annotation { "Feature Type Name" : "Feature", "Feature Type Description" : "" }
export const myFeature = defineFeature(function(context is Context, id is Id, definition is map)
    precondition{}
    {
        {
            var Q0;
            Q0=qCreatedBy(makeId("Front.planeOp"),FACE);
            var sketch = newSketch(context, id + "F0", { "sketchPlane" : qUnion([Q0])});
            skLineSegment(sketch, "E0.bottom", {"start": v(-44.45, 25.4) * mm, "end": v(44.45, 25.4) * mm});
            skLineSegment(sketch, "E0.top", {"start": v(-44.45, -25.4) * mm, "end": v(44.45, -25.4) * mm});
            skLineSegment(sketch, "E0.left", {"start": v(-44.45, 25.4) * mm, "end": v(-44.45, -25.4) * mm});
            skLineSegment(sketch, "E0.right", {"start": v(44.45, 25.4) * mm, "end": v(44.45, -25.4) * mm});
            skPoint(sketch, "E0.middle", {"position": v(0, 0) * mm});
            skLineSegment(sketch, "E1", {"start": v(0, 0) * mm, "end": v(44.45, 0) * mm, "construction": true});
            skCircle(sketch, "E2", {"center": v(29.84, 10.8) * mm, "radius": 6.99 * mm});
            skCircle(sketch, "E3.0", {"center": v(29.84, 10.8) * mm, "radius": 14.6 * mm});
            skLineSegment(sketch, "E4", {"start": v(17.02, 17.78) * mm, "end": v(29.84, 17.78) * mm});
            skLineSegment(sketch, "E5", {"start": v(17.02, 17.78) * mm, "end": v(17.02, 3.81) * mm});
            skLineSegment(sketch, "E6", {"start": v(17.02, 3.81) * mm, "end": v(29.85, 3.81) * mm});
            skCircle(sketch, "E7.MirrorC", {"center": v(29.84, -10.8) * mm, "radius": 6.99 * mm});
            skLineSegment(sketch, "E8.MirrorCS", {"start": v(17.02, -17.78) * mm, "end": v(29.84, -17.78) * mm});
            skCircle(sketch, "E9.MirrorC", {"center": v(29.84, -10.8) * mm, "radius": 14.6 * mm});
            skLineSegment(sketch, "E10.MirrorCS", {"start": v(17.02, -17.78) * mm, "end": v(17.02, -3.81) * mm});
            skLineSegment(sketch, "E11.MirrorCS", {"start": v(17.02, -3.81) * mm, "end": v(29.85, -3.81) * mm});
            skSolve(sketch);
        }
        {
            var Q0;
            {var subQ5=sQuery(id+"F0.wireOp",EDGE,"E0.left");Q0=makeQuery(id+"F0.imprint","IMPRINT",FACE,{"disambiguationData":[TD([[makeQuery(id+"F0.imprint","IMPRINT",EDGE,{"derivedFrom":subQ5}),1.0]])]});}
            var Q1;
            {var subQ4=sQuery(id+"F0.wireOp",EDGE,"E4");Q1=makeQuery(id+"F0.imprint","IMPRINT",FACE,{"disambiguationData":[TD([[makeQuery(id+"F0.imprint","IMPRINT",EDGE,{"derivedFrom":subQ4}),1.0]])]});}
            var Q2;
            {var subQ0=sQuery(id+"F0.wireOp",EDGE,"E5");Q2=makeQuery(id+"F0.imprint","IMPRINT",FACE,{"disambiguationData":[TD([[makeQuery(id+"F0.imprint","IMPRINT",EDGE,{"derivedFrom":subQ0}),-1.0]])]});}
            var Q3;
            {var subQ0=sQuery(id+"F0.wireOp",EDGE,"E6");Q3=makeQuery(id+"F0.imprint","IMPRINT",FACE,{"disambiguationData":[TD([[makeQuery(id+"F0.imprint","IMPRINT",EDGE,{"derivedFrom":subQ0}),-1.0]])]});}
            var Q4;
            {var subQ0=sQuery(id+"F0.wireOp",EDGE,"E3.0");var subQ2=sQuery(id+"F0.wireOp",EDGE,"E9.MirrorC");var subQ3=makeQuery(id+"F0.imprint","INTERSECT",VERTEX,{"disambiguationData":[OD(0.0)],"derivedFrom":[subQ0,subQ2]});Q4=makeQuery(id+"F0.imprint","IMPRINT",FACE,{"disambiguationData":[TD([[makeQuery(id+"F0.imprint","IMPRINT",EDGE,{"disambiguationData":[TD([[subQ3,-1.0]])],"derivedFrom":subQ0}),1.0]])]});}
            var Q5;
            {var subQ3=sQuery(id+"F0.wireOp",EDGE,"E8.MirrorCS");Q5=makeQuery(id+"F0.imprint","IMPRINT",FACE,{"disambiguationData":[TD([[makeQuery(id+"F0.imprint","IMPRINT",EDGE,{"derivedFrom":subQ3}),-1.0]])]});}
            var Q6;
            {var subQ0=sQuery(id+"F0.wireOp",EDGE,"E11.MirrorCS");Q6=makeQuery(id+"F0.imprint","IMPRINT",FACE,{"disambiguationData":[TD([[makeQuery(id+"F0.imprint","IMPRINT",EDGE,{"derivedFrom":subQ0}),1.0]])]});}
            var Q7;
            {var subQ0=sQuery(id+"F0.wireOp",EDGE,"E10.MirrorCS");Q7=makeQuery(id+"F0.imprint","IMPRINT",FACE,{"disambiguationData":[TD([[makeQuery(id+"F0.imprint","IMPRINT",EDGE,{"derivedFrom":subQ0}),1.0]])]});}
            extrude(context, id + "F1", {"entities" : qUnion([Q0, Q1, Q2, Q3, Q4, Q5, Q6, Q7]), "depth" : 0.38 * mm});
        }
        {
            var Q0;
            Q0=makeQuery(id+"F1.opExtrude","CAP_FACE",FACE,{"disambiguationData":[OSD([sQuery(id+"F0.wireOp",EDGE,"E0.bottom"),sQuery(id+"F0.wireOp",EDGE,"E0.top"),sQuery(id+"F0.wireOp",EDGE,"E0.left"),sQuery(id+"F0.wireOp",EDGE,"E2"),sQuery(id+"F0.wireOp",EDGE,"E3.0"),sQuery(id+"F0.wireOp",EDGE,"E4"),sQuery(id+"F0.wireOp",EDGE,"E5"),sQuery(id+"F0.wireOp",EDGE,"E6"),sQuery(id+"F0.wireOp",EDGE,"E7.MirrorC"),sQuery(id+"F0.wireOp",EDGE,"E8.MirrorCS"),sQuery(id+"F0.wireOp",EDGE,"E9.MirrorC"),sQuery(id+"F0.wireOp",EDGE,"E10.MirrorCS"),sQuery(id+"F0.wireOp",EDGE,"E11.MirrorCS")])],"isStart":false});
            var sketch = newSketch(context, id + "F2", { "sketchPlane" : qUnion([Q0])});
            skText(sketch, "E12", { "text": "Ben Bernstein", "fontName": "Tinos-Regular.ttf"});
            skText(sketch, "E13", { "text": "Mechanical Engineer", "fontName": "Tinos-Regular.ttf"});
            skText(sketch, "E14", { "text": "610-715-3790\<email>\nhttp://benbernstein.me", "fontName": "Tinos-Regular.ttf"});
            skLineSegment(sketch, "E15.bottom", {"start": v(-38.1, -7.62) * mm, "end": v(-6.35, -7.62) * mm, "construction": true});
            skLineSegment(sketch, "E15.top", {"start": v(-38.1, -19.05) * mm, "end": v(-6.35, -19.05) * mm, "construction": true});
            skLineSegment(sketch, "E15.left", {"start": v(-38.1, -7.62) * mm, "end": v(-38.1, -19.05) * mm, "construction": true});
            skLineSegment(sketch, "E15.right", {"start": v(-6.35, -7.62) * mm, "end": v(-6.35, -19.05) * mm, "construction": true});
            const initialGuessF2  = {"E12": [-0.0381, 0.01348, 1, 0, 0.00557], "E13": [-0.0381, 0.00823, 1, 0, 0.0032], "E14": [-0.0381, -0.01016, 1, 0, 0.00254]};
            skSetInitialGuess(sketch, initialGuessF2);
            skSolve(sketch);
        }
        {
            var Q0;
            Q0=qSketchRegion(id+"F2",true);
            extrude(context, id + "F3", {"entities" : qUnion([Q0]), "operationType" : NewBodyOperationType.REMOVE, "oppositeDirection" : true, "depth" : 0.08 * mm});
        }
        {
            var Q0;
            {var subQ0=sQuery(id+"F0.wireOp",EDGE,"E6");var subQ1=sQuery(id+"F0.wireOp",EDGE,"E11.MirrorCS");var subQ2=sQuery(id+"F0.wireOp",EDGE,"E5");var subQ3=sQuery(id+"F0.wireOp",EDGE,"E3.0");var subQ4=sQuery(id+"F0.wireOp",EDGE,"E0.bottom");var subQ5=sQuery(id+"F0.wireOp",EDGE,"E7.MirrorC");var subQ6=sQuery(id+"F0.wireOp",EDGE,"E2");var subQ7=sQuery(id+"F0.wireOp",EDGE,"E0.left");var subQ8=sQuery(id+"F0.wireOp",EDGE,"E10.MirrorCS");var subQ9=sQuery(id+"F0.wireOp",EDGE,"E9.MirrorC");var subQ10=sQuery(id+"F0.wireOp",EDGE,"E4");var subQ11=sQuery(id+"F0.wireOp",EDGE,"E8.MirrorCS");var subQ12=sQuery(id+"F0.wireOp",EDGE,"E0.top");Q0=makeQuery(id+"F3.boolean.opBoolean","SPLIT",FACE,{"disambiguationData":[TD([makeQuery(id+"F1.opExtrude","SWEPT_FACE",FACE,{"disambiguationData":[OSD([subQ4])]})])],"derivedFrom":makeQuery(id+"F1.opExtrude","CAP_FACE",FACE,{"disambiguationData":[OSD([subQ4,subQ12,subQ7,subQ6,subQ3,subQ10,subQ2,subQ0,subQ5,subQ11,subQ9,subQ8,subQ1])],"isStart":false})});}
            var sketch = newSketch(context, id + "F4", { "sketchPlane" : qUnion([Q0])});
            skLineSegment(sketch, "E16", {"start": v(-41.9, 22.23) * mm, "end": v(-41.91, 5.08) * mm});
            skLineSegment(sketch, "E17", {"start": v(-41.9, 25.4) * mm, "end": v(-42.7, 22.23) * mm});
            skLineSegment(sketch, "E18", {"start": v(-42.7, 22.23) * mm, "end": v(-41.12, 22.23) * mm});
            skLineSegment(sketch, "E19", {"start": v(-41.12, 22.23) * mm, "end": v(-41.91, 25.4) * mm});
            skLineSegment(sketch, "E20.MirrorCS", {"start": v(-41.91, -25.4) * mm, "end": v(-42.7, -22.23) * mm});
            skLineSegment(sketch, "E21.MirrorCS", {"start": v(-42.7, -22.23) * mm, "end": v(-41.12, -22.23) * mm});
            skLineSegment(sketch, "E22.MirrorCS", {"start": v(-41.12, -22.23) * mm, "end": v(-41.91, -25.4) * mm});
            skLineSegment(sketch, "E23", {"start": v(-41.28, -20.32) * mm, "end": v(-5.08, -20.32) * mm});
            skLineSegment(sketch, "E24", {"start": v(-44.45, -20.32) * mm, "end": v(-41.28, -19.53) * mm});
            skLineSegment(sketch, "E25", {"start": v(-41.28, -19.53) * mm, "end": v(-41.28, -21.11) * mm});
            skLineSegment(sketch, "E26", {"start": v(-41.28, -21.11) * mm, "end": v(-44.45, -20.32) * mm});
            skLineSegment(sketch, "E27", {"start": v(17.27, -1.78) * mm, "end": v(12.33, -6.72) * mm});
            skArc(sketch, "E28", {"start": v(19.52, 0.47) * mm, "mid": v(43.34, 5.2) * mm, "end": v(29.85, 25.4) * mm, "construction": true});
            skLineSegment(sketch, "E29", {"start": v(19.52, 0.47) * mm, "end": v(16.71, -1.22) * mm});
            skLineSegment(sketch, "E30", {"start": v(16.71, -1.22) * mm, "end": v(17.83, -2.34) * mm});
            skLineSegment(sketch, "E31", {"start": v(17.83, -2.34) * mm, "end": v(19.52, 0.47) * mm});
            skLineSegment(sketch, "E32", {"start": v(20.08, -0.1) * mm, "end": v(18.96, 1.03) * mm});
            skLineSegment(sketch, "E33", {"start": v(29.85, 20.07) * mm, "end": v(29.85, 18.29) * mm});
            skLineSegment(sketch, "E34", {"start": v(17.02, 20.07) * mm, "end": v(17.02, 18.29) * mm});
            skLineSegment(sketch, "E35", {"start": v(20.2, 19.27) * mm, "end": v(26.67, 19.27) * mm});
            skLineSegment(sketch, "E36", {"start": v(5.08, -20.32) * mm, "end": v(40.92, -20.32) * mm});
            skLineSegment(sketch, "E37", {"start": v(17.02, 19.27) * mm, "end": v(20.2, 20.07) * mm});
            skLineSegment(sketch, "E38", {"start": v(20.2, 20.07) * mm, "end": v(20.2, 18.48) * mm});
            skLineSegment(sketch, "E39", {"start": v(20.2, 18.48) * mm, "end": v(17.02, 19.27) * mm});
            skLineSegment(sketch, "E40", {"start": v(29.84, 19.27) * mm, "end": v(26.67, 20.07) * mm});
            skLineSegment(sketch, "E41", {"start": v(26.67, 20.07) * mm, "end": v(26.67, 18.48) * mm});
            skLineSegment(sketch, "E42", {"start": v(26.67, 18.48) * mm, "end": v(29.84, 19.27) * mm});
            skLineSegment(sketch, "E43", {"start": v(16.51, 17.78) * mm, "end": v(14.73, 17.78) * mm});
            skLineSegment(sketch, "E44", {"start": v(16.51, 3.81) * mm, "end": v(14.73, 3.81) * mm});
            skLineSegment(sketch, "E45", {"start": v(15.62, 6.99) * mm, "end": v(15.62, 14.6) * mm});
            skLineSegment(sketch, "E46", {"start": v(15.62, 17.78) * mm, "end": v(14.83, 14.6) * mm});
            skLineSegment(sketch, "E47", {"start": v(14.83, 14.6) * mm, "end": v(16.42, 14.6) * mm});
            skLineSegment(sketch, "E48", {"start": v(16.42, 14.6) * mm, "end": v(15.62, 17.78) * mm});
            skLineSegment(sketch, "E49", {"start": v(14.83, 6.99) * mm, "end": v(15.62, 3.81) * mm});
            skLineSegment(sketch, "E50", {"start": v(14.83, 6.99) * mm, "end": v(16.42, 6.99) * mm});
            skLineSegment(sketch, "E51", {"start": v(16.42, 6.99) * mm, "end": v(15.62, 3.81) * mm});
            skLineSegment(sketch, "E52.trimOffspring", {"start": v(-41.91, -20.96) * mm, "end": v(-41.91, -22.23) * mm});
            skPoint(sketch, "E53.start.orphan", {"position": v(-41.91, -5.08) * mm});
            skLineSegment(sketch, "E54", {"start": v(-41.91, -5.08) * mm, "end": v(-41.91, -19.69) * mm});
            skSolve(sketch);
        }
        {
            var Q0;
            {var subQ1=sQuery(id+"F4.wireOp",EDGE,"E19");Q0=makeQuery(id+"F4.imprint","IMPRINT",FACE,{"disambiguationData":[TD([[makeQuery(id+"F4.imprint","IMPRINT",EDGE,{"derivedFrom":subQ1}),-1.0]])]});}
            var sketch = newSketch(context, id + "F5", { "sketchPlane" : qUnion([Q0])});
            skText(sketch, "E55", { "text": "3.50", "fontName": "NotoSansCJKjp-Regular.otf"});
            skLineSegment(sketch, "E56", {"start": v(-3.8, -20.32) * mm, "end": v(-5.08, -20.32) * mm, "construction": true});
            skText(sketch, "E57", { "text": "2.00", "fontName": "OpenSans-Regular.ttf"});
            skLineSegment(sketch, "E58", {"start": v(-41.91, -3.81) * mm, "end": v(-41.91, -5.08) * mm, "construction": true});
            skText(sketch, "E59", { "text": "Ø1.15", "fontName": "OpenSans-Regular.ttf"});
            skLineSegment(sketch, "E60", {"start": v(11.44, -7.61) * mm, "end": v(12.33, -6.72) * mm, "construction": true});
            skText(sketch, "E61", { "text": "0.50", "fontName": "OpenSans-Regular.ttf"});
            skText(sketch, "E62", { "text": "0.55", "fontName": "OpenSans-Regular.ttf"});
            const initialGuessF5  = {"E55": [-0.0038, -0.02173, 1, 0, 0.00281], "E57": [-0.04054, -0.00381, 0, 1, 0.00275], "E59": [0.00494, -0.01605, 0.7071, 0.7071, 0.00275], "E61": [0.01962, 0.02054, 1, 0, 0.00275], "E62": [0.01435, 0.00699, 0, 1, 0.00276]};
            skSetInitialGuess(sketch, initialGuessF5);
            skSolve(sketch);
        }
        {
            var Q0;
            Q0=qSketchRegion(id+"F5",true);
            extrude(context, id + "F6", {"entities" : qUnion([Q0]), "operationType" : NewBodyOperationType.REMOVE, "oppositeDirection" : true, "depth" : 0.08 * mm});
        }
    });